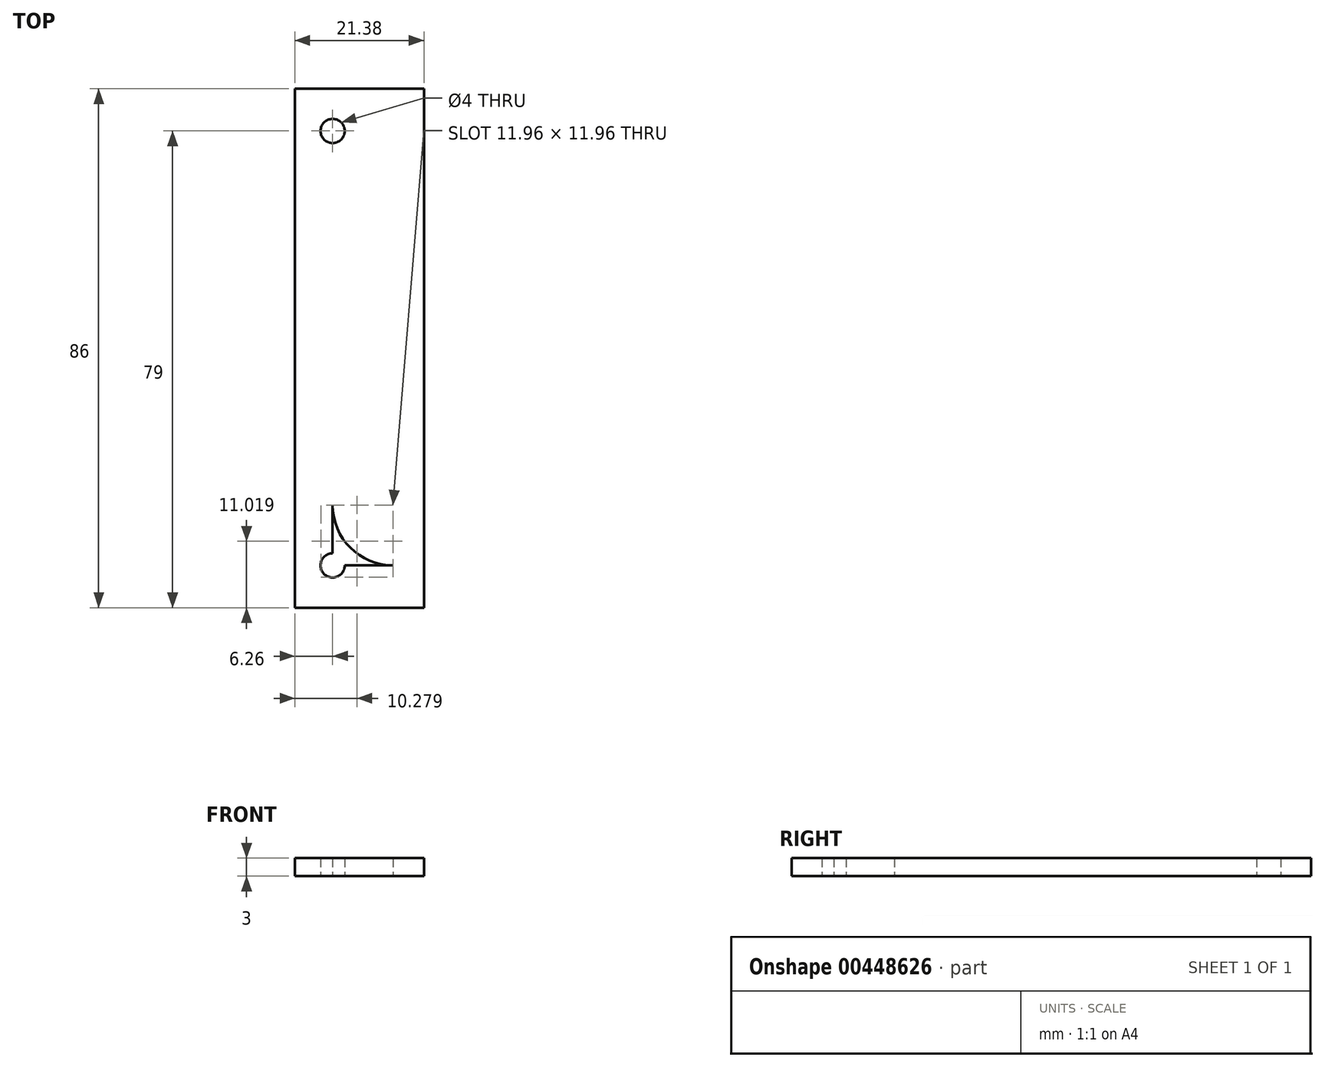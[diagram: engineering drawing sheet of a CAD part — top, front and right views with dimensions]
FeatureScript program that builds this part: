
annotation { "Feature Type Name" : "Feature", "Feature Type Description" : "" }
export const myFeature = defineFeature(function(context is Context, id is Id, definition is map)
    precondition{}
    {
        {
            var Q0;
            Q0=qCreatedBy(makeId("Top.planeOp"),FACE);
            var sketch = newSketch(context, id + "F0", { "sketchPlane" : qUnion([Q0])});
            skLineSegment(sketch, "E0.bottom", {"start": v(86.5, 36) * mm, "end": v(-86.5, 36) * mm});
            skLineSegment(sketch, "E0.top", {"start": v(86.5, -36) * mm, "end": v(-86.5, -36) * mm});
            skLineSegment(sketch, "E0.left", {"start": v(86.5, 36) * mm, "end": v(86.5, -36) * mm});
            skLineSegment(sketch, "E0.right", {"start": v(-86.5, 36) * mm, "end": v(-86.5, -36) * mm});
            skPoint(sketch, "E0.middle", {"position": v(0, 0) * mm});
            skLineSegment(sketch, "E1.bottom", {"start": v(102, 52) * mm, "end": v(-102, 52) * mm});
            skLineSegment(sketch, "E1.top", {"start": v(102, -52) * mm, "end": v(-102, -52) * mm});
            skLineSegment(sketch, "E1.left", {"start": v(102, 52) * mm, "end": v(102, -52) * mm});
            skLineSegment(sketch, "E1.right", {"start": v(-102, 52) * mm, "end": v(-102, -52) * mm});
            skCircle(sketch, "E2", {"center": v(-86.5, 36) * mm, "radius": 2 * mm});
            skArc(sketch, "E3", {"start": v(-76.5, 36) * mm, "mid": v(-83.57, 33.07) * mm, "end": v(-86.5, 26) * mm});
            skArc(sketch, "E4.MirrorCS", {"start": v(-76.5, -36) * mm, "mid": v(-83.57, -33.07) * mm, "end": v(-86.5, -26) * mm});
            skCircle(sketch, "E5.MirrorC", {"center": v(-86.5, -36) * mm, "radius": 2 * mm});
            skArc(sketch, "E6.MirrorCS", {"start": v(76.5, 36) * mm, "mid": v(83.57, 33.07) * mm, "end": v(86.5, 26) * mm});
            skCircle(sketch, "E7.MirrorC", {"center": v(86.5, 36) * mm, "radius": 2 * mm});
            skArc(sketch, "E8.MirrorCS", {"start": v(76.5, -36) * mm, "mid": v(83.57, -33.07) * mm, "end": v(86.5, -26) * mm});
            skCircle(sketch, "E9.MirrorC", {"center": v(86.5, -36) * mm, "radius": 2 * mm});
            skLineSegment(sketch, "E10", {"start": v(-71.38, 36) * mm, "end": v(-71.38, -36) * mm});
            skLineSegment(sketch, "E11.MirrorCS", {"start": v(71.38, 36) * mm, "end": v(71.38, -36) * mm});
            skLineSegment(sketch, "E12", {"start": v(-71.38, 36) * mm, "end": v(-71.38, 43) * mm});
            skLineSegment(sketch, "E13", {"start": v(-71.38, 43) * mm, "end": v(-92.76, 43) * mm});
            skLineSegment(sketch, "E14", {"start": v(-92.76, 43) * mm, "end": v(-92.76, -43) * mm});
            skLineSegment(sketch, "E15", {"start": v(-92.76, -43) * mm, "end": v(-71.38, -43) * mm});
            skLineSegment(sketch, "E16", {"start": v(-71.38, -43) * mm, "end": v(-71.38, -36) * mm});
            skSolve(sketch);
        }
        {
            var Q0;
            {var subQ14=sQuery(id+"F0.wireOp",EDGE,"E12");Q0=makeQuery(id+"F0.imprint","IMPRINT",FACE,{"disambiguationData":[TD([[makeQuery(id+"F0.imprint","IMPRINT",EDGE,{"derivedFrom":subQ14}),1.0]])]});}
            var Q1;
            {var subQ0=sQuery(id+"F0.wireOp",EDGE,"E3");Q1=makeQuery(id+"F0.imprint","IMPRINT",FACE,{"disambiguationData":[TD([[makeQuery(id+"F0.imprint","IMPRINT",EDGE,{"derivedFrom":subQ0}),-1.0]])]});}
            var Q2;
            {var subQ0=sQuery(id+"F0.wireOp",EDGE,"E4.MirrorCS");Q2=makeQuery(id+"F0.imprint","IMPRINT",FACE,{"disambiguationData":[TD([[makeQuery(id+"F0.imprint","IMPRINT",EDGE,{"derivedFrom":subQ0}),1.0]])]});}
            extrude(context, id + "F1", {"entities" : qUnion([Q0, Q1, Q2]), "depth" : 3 * mm});
        }
        {
            var Q0;
            {var subQ0=sQuery(id+"F0.wireOp",EDGE,"E3");Q0=makeQuery(id+"F0.imprint","IMPRINT",FACE,{"disambiguationData":[TD([[makeQuery(id+"F0.imprint","IMPRINT",EDGE,{"derivedFrom":subQ0}),1.0]])]});}
            extrude(context, id + "F2", {"entities" : qUnion([Q0]), "operationType" : NewBodyOperationType.ADD, "depth" : 1.4 * mm});
        }
    });
